# Revit family: Hager-VEGA-Surface_mounted-IP40-With_Cover-With_DIN-Hosted-PL-en
name_source: partatom
category: Electrical Equipment
units: mm (PartAtom-declared; Revit-internal decimal feet)

## family parameters
Cut with Voids When Loaded = No
Host = Face
Maintain Annotation Orientation = Yes
Panel Configuration = Two Columns, Circuits Across
Part Type = Panelboard
Room Calculation Point = No
Round Connector Dimension = Use Diameter
Shared = No

## types (11) — shared parameters
BC_MODEL_ID = 1547040
BC_OBJECT_ID = 513451
BC_OBJECT_VERSION = #5
Code hager = ADD-EC000214_EU
EF000003 - Mounting method = Surface mounted
EF000007 - Colour = White
EF000008 - Width = 400 mm  [stored 1.31234 ft]
EF000024 - UV resistant = No
EF000049 - Depth = 146 mm  [stored 0.479003 ft]
EF000116 - RAL-number = 9010
EF001062 - EMC-version = No
EF001088 - Extension possible = Yes
EF001134 - DIN-rail = Yes
EF002950 - Width in number of modular spacings = 18
EF004462 - Type of closure = Other
EF005474 - Degree of protection (IP) = IP40
EF006306 - With lock = No
EF015776 - Earthing terminal block = Yes
EF015941 - Signal passing door = Yes
ETIM class code = EC000214
ETIM class name = Small distribution board
HG000002-With door or cover = Yes
HG000003-Range = VEGA
HG000005-Thickness = 2 mm  [stored 0.00656168 ft]
HG000006-Flush mounted = No
HG000009-Double swing door = No
HG000010-Asymmetric doors = No
HG000011-Empty rows from bottom = No
HG000012-Door swing angle = 90.00°
HG000013-Door on the left = No
HG000014-Door on the right = Yes
HG000015-Clearance visibility = Yes
HG000016-Door 3D visibility = Yes
HG000017-Distance between poles = 18 mm  [stored 0.0590551 ft]
HG000060-RAL-number = 9010
HG000099-Onfly Template ID = 507532
HGEF002950-Width in number of modular spacings = 18
Manufacturer = Hager
Name = VEGA-Surface_mounted-IP40-With_Cover-With_DIN-PL
Name BIM&CO = Electricity
Name hager = ADD_Enclosures_EC000214
Uniformat = Low Tension Service & Dist.
Uniformat code = D501001
zero-valued in all types: Default Elevation, EF000218 - Built-in depth, EF000332 - Built-in height, EF000846 - Built-in width, EF001131 - Inner depth, HG000007-Number of empty columns, HG000008-Number of empty rows

## per-type parameters (varying)
| type | BC_VARIANT_ID | EF000040 - Height | EF000118 - With mounting plate | EF000266 - Number of rows | EF006244 - Transparent cover/door | EF009212 - Cover model | EF015777 - Neutral terminal block | HG000001-Number of columns | HG000004-Manufacturer reference | HGEF000266-Number of rows |
| VEGA-Surface_mounted_W400_H325_D146_18_Modular_Spacing-VB118MP | 1174002 | 325 mm  [stored 1.06627 ft] | Yes | 0 | No | With notch | No | 0 | VB118MP | 0 |
| VEGA-Surface_mounted_W400_H325_D146_18_Modular_Spacing-VB118PB | 1174003 | 325 mm  [stored 1.06627 ft] | No | 1 | No | Closed | Yes | 1 | VB118PB | 1 |
| VEGA-Surface_mounted_W400_H325_D146_18_Modular_Spacing-VB118TB | 1174004 | 325 mm  [stored 1.06627 ft] | No | 1 | Yes | Closed | Yes | 1 | VB118TB | 1 |
| VEGA-Surface_mounted_W400_H475_D146_18_Modular_Spacing-VB218MP | 1174005 | 475 mm  [stored 1.5584 ft] | Yes | 0 | No | With notch | No | 0 | VB218MP | 0 |
| VEGA-Surface_mounted_W400_H475_D146_18_Modular_Spacing-VB218PB | 1174006 | 475 mm  [stored 1.5584 ft] | No | 2 | No | Closed | Yes | 1 | VB218PB | 2 |
| VEGA-Surface_mounted_W400_H475_D146_18_Modular_Spacing-VB218TB | 1174007 | 475 mm  [stored 1.5584 ft] | No | 2 | Yes | Closed | Yes | 1 | VB218TB | 2 |
| VEGA-Surface_mounted_W400_H625_D146_18_Modular_Spacing-VB318MP | 1174008 | 625 mm  [stored 2.05052 ft] | Yes | 0 | No | With notch | No | 0 | VB318MP | 0 |
| VEGA-Surface_mounted_W400_H625_D146_18_Modular_Spacing-VB318PB | 1174009 | 625 mm  [stored 2.05052 ft] | No | 3 | No | Closed | Yes | 1 | VB318PB | 3 |
| VEGA-Surface_mounted_W400_H625_D146_18_Modular_Spacing-VB318TB | 1174010 | 625 mm  [stored 2.05052 ft] | No | 3 | Yes | Closed | Yes | 1 | VB318TB | 3 |
| VEGA-Surface_mounted_W400_H775_D146_18_Modular_Spacing-VB418PB | 1174011 | 775 mm  [stored 2.54265 ft] | No | 4 | No | Closed | Yes | 1 | VB418PB | 4 |
| VEGA-Surface_mounted_W400_H775_D146_18_Modular_Spacing-VB418TB | 1174012 | 775 mm  [stored 2.54265 ft] | No | 4 | Yes | Closed | Yes | 1 | VB418TB | 4 |

note: column(s) folded — value = type name in every type: Reference

note: [stored X ft] marks values corroborated as IEEE doubles in the binary element streams (Revit-internal decimal feet)

## geometry (parser evidence)
native form markers: Sweep x14
no freeform markers — native parametric forms only
